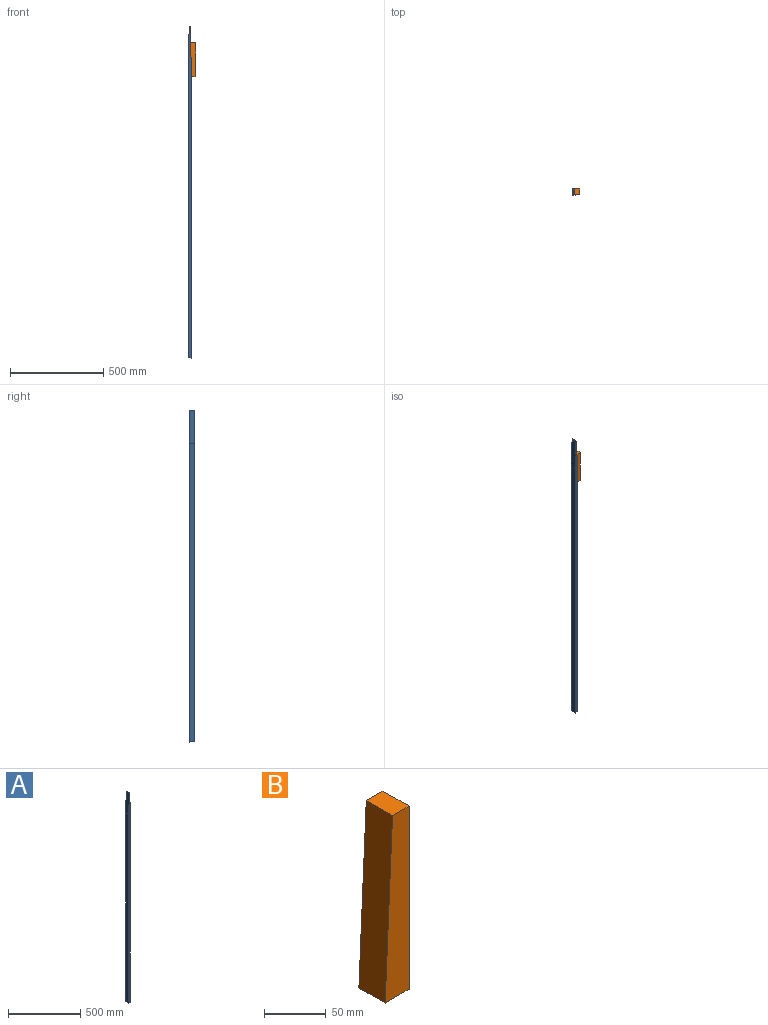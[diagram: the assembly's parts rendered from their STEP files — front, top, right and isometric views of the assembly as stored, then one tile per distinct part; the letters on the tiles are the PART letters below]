
ASSEMBLY  parts=2 mates=1
PART A: 10 faces, bbox 15x30x1780 mm
  f0: plane 30x0.01mm, normal (0,0,1), area 0.2mm2, adj f1,f7,f8,f9
  f1: plane 180x30mm, normal (1,0,0.03), area 5402.1mm2, adj f0,f2,f8,f9
  f2: plane 30x2.5mm, normal (0,0,1), area 75mm2, adj f1,f3,f8,f9
  f3: plane 30x2.5mm, normal (0.01,0,1), area 75mm2, adj f2,f4,f8,f9
  f4: plane 180.02x30mm, normal (-1,0,0.03), area 5402.6mm2, adj f3,f5,f8,f9
  f5: plane 1600x30mm, normal (-1,0,0), area 48000mm2, adj f4,f6,f8,f9
  f6: plane 30x15.01mm, normal (0,0,-1), area 450.2mm2, adj f5,f7,f8,f9
  f7: plane 1600x30mm, normal (1,0,0), area 48000mm2, adj f0,f6,f8,f9
  f8: plane 1780.02x15.01mm, normal (0,-1,0), area 25811.4mm2, adj f0,f1,f2,f3,f4,f5,f6,f7
  f9: plane 1780.02x15.01mm, normal (0,1,0), area 25811.4mm2, adj f0,f1,f2,f3,f4,f5,f6,f7
PART B: 6 faces, bbox 27.4x30x181.1 mm
  f0: plane 181.12x30mm, normal (-1,0,0.05), area 5439.4mm2, adj f1,f3,f4,f5
  f1: plane 30x27.37mm, normal (0,0,-1), area 821mm2, adj f0,f2,f4,f5
  f2: plane 181.12x30mm, normal (1,0,0), area 5433.5mm2, adj f1,f3,f4,f5
  f3: plane 30x18.95mm, normal (0,0,1), area 568.4mm2, adj f0,f2,f4,f5
  f4: plane 181.12x27.37mm, normal (0,-1,0), area 4194.1mm2, adj f0,f1,f2,f3
  f5: plane 181.12x27.37mm, normal (0,1,0), area 4194.1mm2, adj f0,f1,f2,f3
PLACE A t=(71.71,-325.09,333.79)mm
PLACE B rot(axis=(1,0,-0.01),180deg) t=(2.28,-355.09,425.8)mm
MATE fastened B.f0 <-> A.f1  axis (-1,0,-0.03) through (79.21,-340.09,333.79)mm
